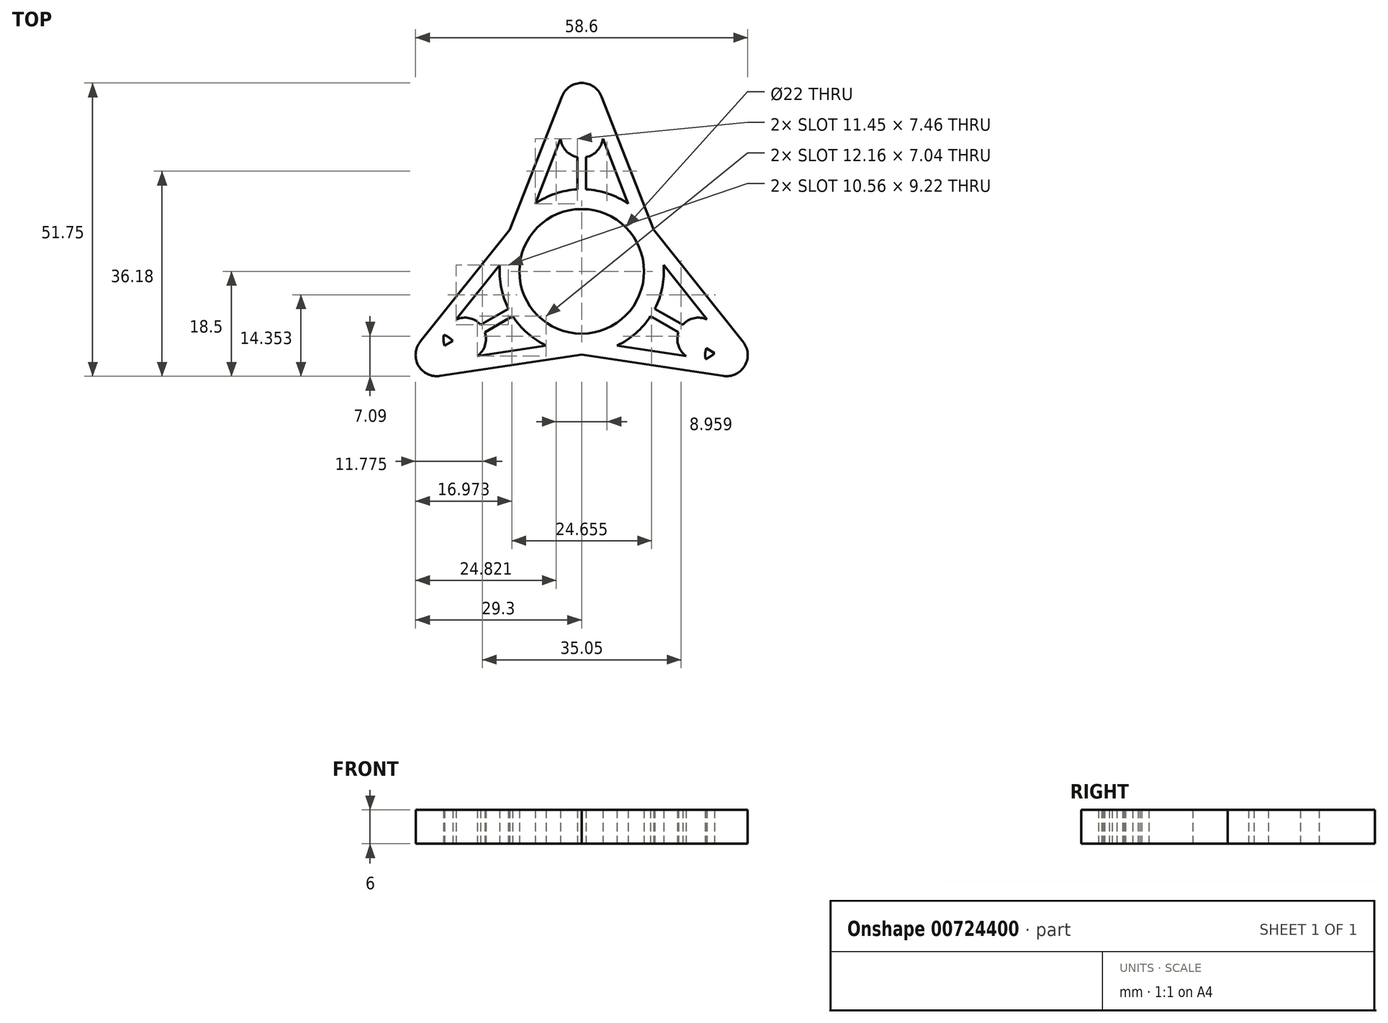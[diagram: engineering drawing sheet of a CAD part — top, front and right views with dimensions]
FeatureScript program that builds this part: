
annotation { "Feature Type Name" : "Feature", "Feature Type Description" : "" }
export const myFeature = defineFeature(function(context is Context, id is Id, definition is map)
    precondition{}
    {
        {
            var Q0;
            Q0=qCreatedBy(makeId("Top.planeOp"),FACE);
            var sketch = newSketch(context, id + "F0", { "sketchPlane" : qUnion([Q0])});
            skCircle(sketch, "E0", {"center": v(0, 0) * mm, "radius": 11 * mm});
            skArc(sketch, "E1", {"start": v(-12.17, -7.89) * mm, "mid": v(-9.57, -10.9) * mm, "end": v(-6.25, -13.09) * mm});
            skLineSegment(sketch, "E2", {"start": v(0, 40.81) * mm, "end": v(0, -43.66) * mm, "construction": true});
            skLineSegment(sketch, "E3", {"start": v(54.3, -31.35) * mm, "end": v(-41.87, 24.17) * mm, "construction": true});
            skLineSegment(sketch, "E4", {"start": v(-54.3, -31.35) * mm, "end": v(45.05, 26.01) * mm, "construction": true});
            skArc(sketch, "E5", {"start": v(3.5, 30.87) * mm, "mid": v(0, 33.25) * mm, "end": v(-3.5, 30.87) * mm});
            skCircle(sketch, "E6.1.0", {"center": v(-25.55, -14.75) * mm, "radius": 3.75 * mm});
            skCircle(sketch, "E6.2.0", {"center": v(25.55, -14.75) * mm, "radius": 3.75 * mm});
            skPoint(sketch, "E7", {"position": v(0, 33.25) * mm});
            skLineSegment(sketch, "E8", {"start": v(3.5, 30.87) * mm, "end": v(12.7, 7.33) * mm});
            skLineSegment(sketch, "E9", {"start": v(2.45, 26.66) * mm, "end": v(8.2, 11.95) * mm});
            skArc(sketch, "E10", {"start": v(2.45, 26.66) * mm, "mid": v(1.66, 27.2) * mm, "end": v(0.75, 27.5) * mm});
            skLineSegment(sketch, "E11.MirrorCS", {"start": v(-2.45, 26.66) * mm, "end": v(-8.2, 11.95) * mm});
            skLineSegment(sketch, "E12.MirrorCS", {"start": v(-3.5, 30.87) * mm, "end": v(-12.7, 7.33) * mm});
            skLineSegment(sketch, "E13.MirrorCS", {"start": v(28.48, -12.4) * mm, "end": v(12.7, 7.33) * mm});
            skLineSegment(sketch, "E14.MirrorCS", {"start": v(24.32, -11.2) * mm, "end": v(14.46, 1.13) * mm});
            skLineSegment(sketch, "E15.MirrorCS", {"start": v(-28.48, -12.4) * mm, "end": v(-12.7, 7.33) * mm});
            skLineSegment(sketch, "E16.MirrorCS", {"start": v(-24.32, -11.2) * mm, "end": v(-14.46, 1.13) * mm});
            skLineSegment(sketch, "E17.MirrorCS", {"start": v(-21.86, -15.46) * mm, "end": v(-6.25, -13.09) * mm});
            skLineSegment(sketch, "E18.MirrorCS", {"start": v(-24.99, -18.46) * mm, "end": v(0, -14.67) * mm});
            skLineSegment(sketch, "E19.MirrorCS", {"start": v(21.86, -15.46) * mm, "end": v(6.25, -13.09) * mm});
            skLineSegment(sketch, "E20.MirrorCS", {"start": v(24.99, -18.46) * mm, "end": v(0, -14.67) * mm});
            skArc(sketch, "E21.trimOffspring", {"start": v(-3.73, 23.4) * mm, "mid": v(0, 20.08) * mm, "end": v(3.73, 23.4) * mm});
            skArc(sketch, "E22.trimOffspring", {"start": v(-2.45, 26.66) * mm, "mid": v(0, 25.75) * mm, "end": v(2.45, 26.66) * mm, "construction": true});
            skArc(sketch, "E23.MirrorCS", {"start": v(-21.86, -15.46) * mm, "mid": v(-22.72, -15.03) * mm, "end": v(-23.44, -14.4) * mm});
            skArc(sketch, "E24.MirrorCS", {"start": v(-22.13, -8.48) * mm, "mid": v(-17.39, -10.04) * mm, "end": v(-18.4, -14.93) * mm});
            skArc(sketch, "E25.MirrorCS", {"start": v(24.32, -11.2) * mm, "mid": v(24.38, -12.16) * mm, "end": v(24.2, -13.1) * mm});
            skArc(sketch, "E26.MirrorCS", {"start": v(18.4, -14.93) * mm, "mid": v(17.39, -10.04) * mm, "end": v(22.13, -8.48) * mm});
            skLineSegment(sketch, "E27", {"start": v(-0.75, 27.5) * mm, "end": v(-0.75, 14.48) * mm});
            skLineSegment(sketch, "E28.MirrorCS", {"start": v(0.75, 27.5) * mm, "end": v(0.75, 14.48) * mm});
            skLineSegment(sketch, "E29.MirrorCS", {"start": v(24.2, -13.1) * mm, "end": v(12.92, -6.6) * mm});
            skLineSegment(sketch, "E30.MirrorCS", {"start": v(23.44, -14.4) * mm, "end": v(12.17, -7.89) * mm});
            skLineSegment(sketch, "E31.MirrorCS", {"start": v(-24.2, -13.1) * mm, "end": v(-12.92, -6.6) * mm});
            skLineSegment(sketch, "E32.MirrorCS", {"start": v(-23.44, -14.4) * mm, "end": v(-12.17, -7.89) * mm});
            skArc(sketch, "E33.trimOffspring", {"start": v(-24.2, -13.1) * mm, "mid": v(-24.38, -12.16) * mm, "end": v(-24.32, -11.2) * mm});
            skArc(sketch, "E34.trimOffspring", {"start": v(23.44, -14.4) * mm, "mid": v(22.72, -15.03) * mm, "end": v(21.86, -15.46) * mm});
            skArc(sketch, "E35.trimOffspring", {"start": v(12.92, -6.6) * mm, "mid": v(14.22, -2.84) * mm, "end": v(14.46, 1.13) * mm});
            skArc(sketch, "E36.trimOffspring", {"start": v(-0.75, 14.48) * mm, "mid": v(-4.65, 13.73) * mm, "end": v(-8.2, 11.95) * mm});
            skArc(sketch, "E37.trimOffspring", {"start": v(-0.75, 27.5) * mm, "mid": v(-1.66, 27.2) * mm, "end": v(-2.45, 26.66) * mm});
            skArc(sketch, "E38.trimOffspring", {"start": v(-14.46, 1.13) * mm, "mid": v(-14.2, -2.83) * mm, "end": v(-12.92, -6.6) * mm});
            skPoint(sketch, "E39.orphan", {"position": v(-11.33, 9.05) * mm});
            skPoint(sketch, "E40.orphan", {"position": v(-13.5, 5.28) * mm});
            skArc(sketch, "E41.trimOffspring", {"start": v(6.25, -13.09) * mm, "mid": v(9.57, -10.9) * mm, "end": v(12.17, -7.89) * mm});
            skPoint(sketch, "E42.orphan", {"position": v(2.18, -14.34) * mm});
            skPoint(sketch, "E43.orphan", {"position": v(-2.18, -14.34) * mm});
            skArc(sketch, "E44.trimOffspring", {"start": v(8.2, 11.95) * mm, "mid": v(4.65, 13.71) * mm, "end": v(0.75, 14.48) * mm});
            skPoint(sketch, "E45.orphan", {"position": v(11.33, 9.05) * mm});
            skPoint(sketch, "E46.orphan", {"position": v(13.5, 5.28) * mm});
            skSolve(sketch);
        }
        {
            var Q0;
            {var subQ5=sQuery(id+"F0.wireOp",EDGE,"E23.MirrorCS");Q0=makeQuery(id+"F0.imprint","IMPRINT",FACE,{"disambiguationData":[TD([[makeQuery(id+"F0.imprint","IMPRINT",EDGE,{"derivedFrom":subQ5}),1.0]])]});}
            var Q1;
            Q1=makeQuery(id+"F0.imprint","IMPRINT",FACE,{"disambiguationData":[TD([[makeQuery(id+"F0.imprint","IMPRINT",EDGE,{"derivedFrom":sQuery(id+"F0.wireOp",EDGE,"E0")}),-1.0]])]});
            var Q2;
            {var subQ7=sQuery(id+"F0.wireOp",EDGE,"E25.MirrorCS");Q2=makeQuery(id+"F0.imprint","IMPRINT",FACE,{"disambiguationData":[TD([[makeQuery(id+"F0.imprint","IMPRINT",EDGE,{"derivedFrom":subQ7}),1.0]])]});}
            var Q3;
            {var subQ0=sQuery(id+"F0.wireOp",EDGE,"E15.MirrorCS");var subQ1=sQuery(id+"F0.wireOp",EDGE,"E6.1.0");var subQ2=makeQuery(id+"F0.imprint","INTERSECT",VERTEX,{"derivedFrom":[subQ1,subQ0]});Q3=makeQuery(id+"F0.imprint","IMPRINT",FACE,{"disambiguationData":[TD([[makeQuery(id+"F0.imprint","IMPRINT",EDGE,{"disambiguationData":[TD([[subQ2,-1.0]])],"derivedFrom":subQ0}),-1.0]])]});}
            var Q4;
            {var subQ0=sQuery(id+"F0.wireOp",EDGE,"E33.trimOffspring");Q4=makeQuery(id+"F0.imprint","IMPRINT",FACE,{"disambiguationData":[TD([[makeQuery(id+"F0.imprint","IMPRINT",EDGE,{"derivedFrom":subQ0}),-1.0]])]});}
            var Q5;
            {var subQ1=sQuery(id+"F0.wireOp",EDGE,"E6.1.0");var subQ3=sQuery(id+"F0.wireOp",EDGE,"E31.MirrorCS");var subQ4=makeQuery(id+"F0.imprint","INTERSECT",VERTEX,{"derivedFrom":[subQ1,subQ3]});Q5=makeQuery(id+"F0.imprint","IMPRINT",FACE,{"disambiguationData":[TD([[makeQuery(id+"F0.imprint","IMPRINT",EDGE,{"disambiguationData":[TD([[subQ4,-1.0]])],"derivedFrom":subQ3}),1.0]])]});}
            var Q6;
            {var subQ1=sQuery(id+"F0.wireOp",EDGE,"E6.1.0");var subQ3=sQuery(id+"F0.wireOp",EDGE,"E32.MirrorCS");var subQ4=makeQuery(id+"F0.imprint","INTERSECT",VERTEX,{"derivedFrom":[subQ1,subQ3]});Q6=makeQuery(id+"F0.imprint","IMPRINT",FACE,{"disambiguationData":[TD([[makeQuery(id+"F0.imprint","IMPRINT",EDGE,{"disambiguationData":[TD([[subQ4,-1.0]])],"derivedFrom":subQ3}),-1.0]])]});}
            var Q7;
            {var subQ1=sQuery(id+"F0.wireOp",EDGE,"E6.1.0");var subQ3=sQuery(id+"F0.wireOp",EDGE,"E18.MirrorCS");var subQ4=makeQuery(id+"F0.imprint","INTERSECT",VERTEX,{"derivedFrom":[subQ1,subQ3]});Q7=makeQuery(id+"F0.imprint","IMPRINT",FACE,{"disambiguationData":[TD([[makeQuery(id+"F0.imprint","IMPRINT",EDGE,{"disambiguationData":[TD([[subQ4,-1.0]])],"derivedFrom":subQ3}),1.0]])]});}
            var Q8;
            {var subQ0=sQuery(id+"F0.wireOp",EDGE,"E23.MirrorCS");Q8=makeQuery(id+"F0.imprint","IMPRINT",FACE,{"disambiguationData":[TD([[makeQuery(id+"F0.imprint","IMPRINT",EDGE,{"derivedFrom":subQ0}),-1.0]])]});}
            var Q9;
            {var subQ0=sQuery(id+"F0.wireOp",EDGE,"E32.MirrorCS");var subQ1=sQuery(id+"F0.wireOp",EDGE,"E6.1.0");var subQ2=makeQuery(id+"F0.imprint","INTERSECT",VERTEX,{"derivedFrom":[subQ1,subQ0]});Q9=makeQuery(id+"F0.imprint","IMPRINT",FACE,{"disambiguationData":[TD([[makeQuery(id+"F0.imprint","IMPRINT",EDGE,{"disambiguationData":[TD([[subQ2,-1.0]])],"derivedFrom":subQ1}),-1.0]])]});}
            var Q10;
            {var subQ1=sQuery(id+"F0.wireOp",EDGE,"E6.2.0");var subQ3=sQuery(id+"F0.wireOp",EDGE,"E20.MirrorCS");var subQ4=makeQuery(id+"F0.imprint","INTERSECT",VERTEX,{"derivedFrom":[subQ1,subQ3]});Q10=makeQuery(id+"F0.imprint","IMPRINT",FACE,{"disambiguationData":[TD([[makeQuery(id+"F0.imprint","IMPRINT",EDGE,{"disambiguationData":[TD([[subQ4,-1.0]])],"derivedFrom":subQ3}),-1.0]])]});}
            var Q11;
            {var subQ1=sQuery(id+"F0.wireOp",EDGE,"E6.2.0");var subQ3=sQuery(id+"F0.wireOp",EDGE,"E30.MirrorCS");var subQ4=makeQuery(id+"F0.imprint","INTERSECT",VERTEX,{"derivedFrom":[subQ1,subQ3]});Q11=makeQuery(id+"F0.imprint","IMPRINT",FACE,{"disambiguationData":[TD([[makeQuery(id+"F0.imprint","IMPRINT",EDGE,{"disambiguationData":[TD([[subQ4,-1.0]])],"derivedFrom":subQ3}),1.0]])]});}
            var Q12;
            {var subQ1=sQuery(id+"F0.wireOp",EDGE,"E6.2.0");var subQ3=sQuery(id+"F0.wireOp",EDGE,"E29.MirrorCS");var subQ4=makeQuery(id+"F0.imprint","INTERSECT",VERTEX,{"derivedFrom":[subQ1,subQ3]});Q12=makeQuery(id+"F0.imprint","IMPRINT",FACE,{"disambiguationData":[TD([[makeQuery(id+"F0.imprint","IMPRINT",EDGE,{"disambiguationData":[TD([[subQ4,-1.0]])],"derivedFrom":subQ3}),-1.0]])]});}
            var Q13;
            {var subQ0=sQuery(id+"F0.wireOp",EDGE,"E13.MirrorCS");var subQ1=sQuery(id+"F0.wireOp",EDGE,"E6.2.0");var subQ2=makeQuery(id+"F0.imprint","INTERSECT",VERTEX,{"derivedFrom":[subQ1,subQ0]});Q13=makeQuery(id+"F0.imprint","IMPRINT",FACE,{"disambiguationData":[TD([[makeQuery(id+"F0.imprint","IMPRINT",EDGE,{"disambiguationData":[TD([[subQ2,-1.0]])],"derivedFrom":subQ0}),1.0]])]});}
            var Q14;
            {var subQ0=sQuery(id+"F0.wireOp",EDGE,"E29.MirrorCS");var subQ1=sQuery(id+"F0.wireOp",EDGE,"E6.2.0");var subQ2=makeQuery(id+"F0.imprint","INTERSECT",VERTEX,{"derivedFrom":[subQ1,subQ0]});Q14=makeQuery(id+"F0.imprint","IMPRINT",FACE,{"disambiguationData":[TD([[makeQuery(id+"F0.imprint","IMPRINT",EDGE,{"disambiguationData":[TD([[subQ2,-1.0]])],"derivedFrom":subQ1}),-1.0]])]});}
            var Q15;
            {var subQ12=sQuery(id+"F0.wireOp",EDGE,"E5");Q15=makeQuery(id+"F0.imprint","IMPRINT",FACE,{"disambiguationData":[TD([[makeQuery(id+"F0.imprint","IMPRINT",EDGE,{"derivedFrom":subQ12}),1.0]])]});}
            var Q16;
            {var subQ0=sQuery(id+"F0.wireOp",EDGE,"E37.trimOffspring");Q16=makeQuery(id+"F0.imprint","IMPRINT",FACE,{"disambiguationData":[TD([[makeQuery(id+"F0.imprint","IMPRINT",EDGE,{"derivedFrom":subQ0}),1.0]])]});}
            var Q17;
            {var subQ0=sQuery(id+"F0.wireOp",EDGE,"E10");Q17=makeQuery(id+"F0.imprint","IMPRINT",FACE,{"disambiguationData":[TD([[makeQuery(id+"F0.imprint","IMPRINT",EDGE,{"derivedFrom":subQ0}),1.0]])]});}
            var Q18;
            {var subQ0=sQuery(id+"F0.wireOp",EDGE,"E25.MirrorCS");Q18=makeQuery(id+"F0.imprint","IMPRINT",FACE,{"disambiguationData":[TD([[makeQuery(id+"F0.imprint","IMPRINT",EDGE,{"derivedFrom":subQ0}),-1.0]])]});}
            var Q19;
            {var subQ0=sQuery(id+"F0.wireOp",EDGE,"E34.trimOffspring");Q19=makeQuery(id+"F0.imprint","IMPRINT",FACE,{"disambiguationData":[TD([[makeQuery(id+"F0.imprint","IMPRINT",EDGE,{"derivedFrom":subQ0}),-1.0]])]});}
            extrude(context, id + "F1", {"entities" : qUnion([Q0, Q1, Q2, Q3, Q4, Q5, Q6, Q7, Q8, Q9, Q10, Q11, Q12, Q13, Q14, Q15, Q16, Q17, Q18, Q19]), "depth" : 6 * mm, "offsetDistance" : 25 * mm});
        }
    });
